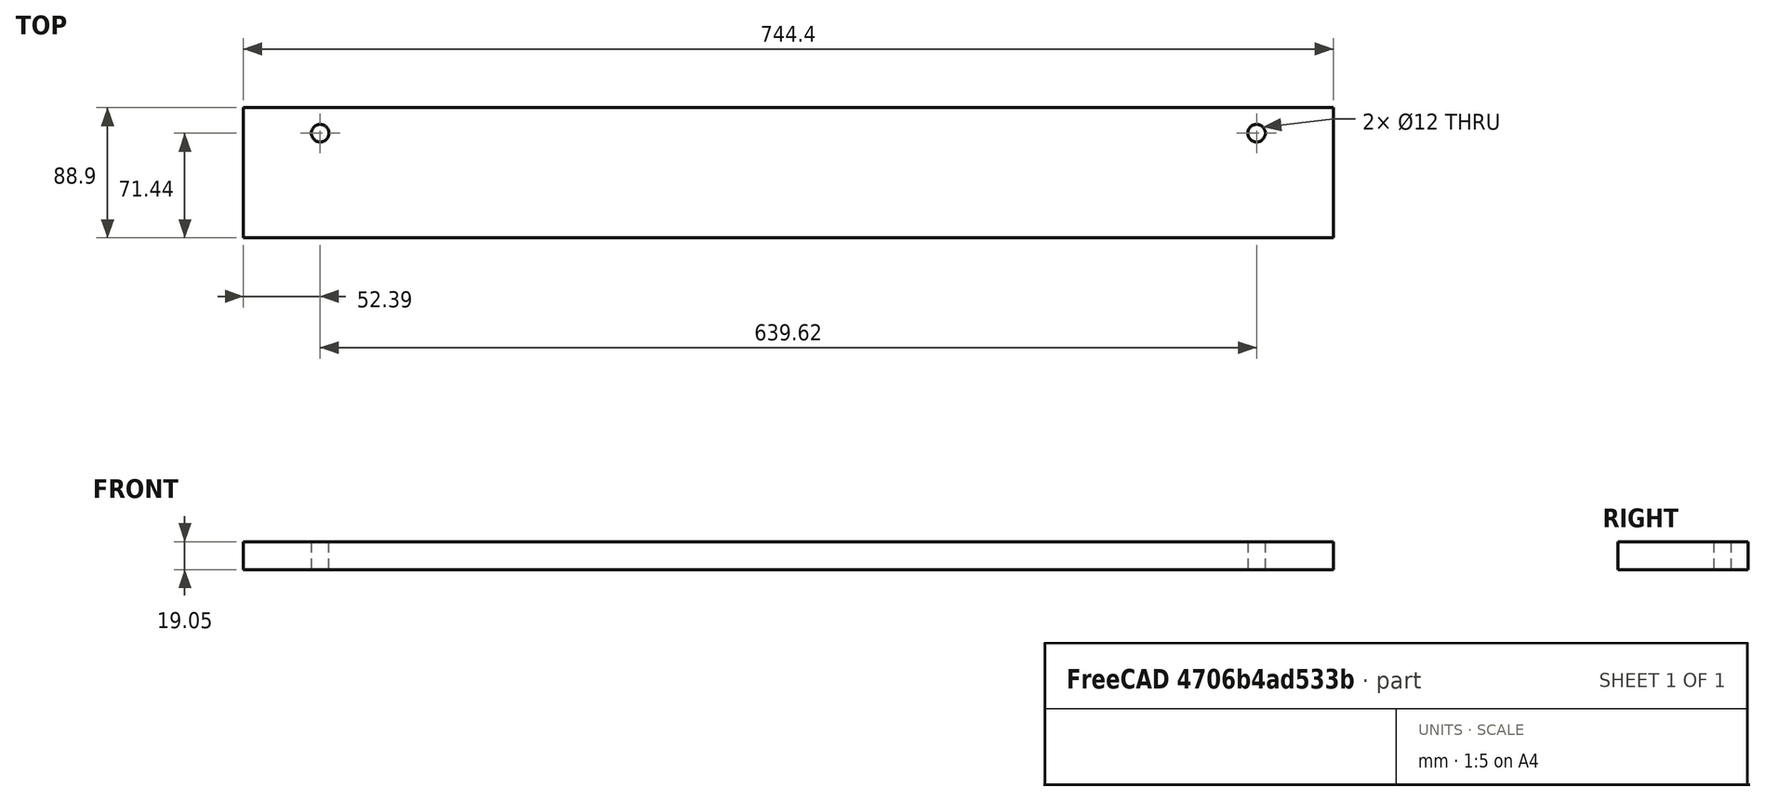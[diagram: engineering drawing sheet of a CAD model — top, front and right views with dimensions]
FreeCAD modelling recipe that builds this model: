
FCSTD DOCUMENT  (FreeCAD 0.19R24291 (Git))
Label: horizontal
License: All rights reserved
LicenseURL: http://en.wikipedia.org/wiki/All_rights_reserved
objects: Sketcher::SketchObject×1, PartDesign::Pad×1, PartDesign::Body×1
note: 4 computed .brp shape members not serialized (recipe doc carries the construction recipe); baked Part::Feature solids carry a one-line shape summary decoded from their .brp

FEATURE [Sketcher::SketchObject] Sketch
  FullyConstrained = true
  MapMode = 5
  Support = -> [XY_Plane]
  expr: Constraints[10] = 3.5 * 25.4
  sketch-geometry (6):
    g0: LineSegment StartX=0 StartY=0 StartZ=0 EndX=744.4 EndY=0 EndZ=0
    g1: LineSegment StartX=744.4 StartY=0 StartZ=0 EndX=744.4 EndY=88.9 EndZ=0
    g2: LineSegment StartX=744.4 StartY=88.9 StartZ=0 EndX=0 EndY=88.9 EndZ=0
    g3: LineSegment StartX=0 StartY=88.9 StartZ=0 EndX=0 EndY=0 EndZ=0
    g4: Circle CenterX=52.39 CenterY=71.44 CenterZ=0 NormalX=0 NormalY=0 NormalZ=1 AngleXU=0 Radius=6
    g5: Circle CenterX=692.01 CenterY=71.44 CenterZ=0 NormalX=0 NormalY=0 NormalZ=1 AngleXU=0 Radius=6
  constraints (17):
    c: Coincident(g0,g1)
    c: Coincident(g1,g2)
    c: Coincident(g2,g3)
    c: Coincident(g3,g0)
    c: Horizontal(g0)
    c: Horizontal(g2)
    c: Vertical(g1)
    c: Vertical(g3)
    c: DistanceX(g0,g0) = 744.4
    c: Coincident(g0,g-1)
    c: DistanceY(g3,g3) = 88.9
    c: DistanceX(g2,g4) = 52.39
    c: DistanceY(g4,g2) = 17.46
    c: Diameter(g4) = 12
    c: Horizontal(g5,g4)
    c: Equal(g5,g4)
    c: DistanceX(g5,g1) = 52.39
FEATURE [PartDesign::Pad] Pad
  Direction = (1,1,1)
  Length = 19.05
  Length2 = 100
  Profile = -> Sketch
  Type = 0
  expr: Length = 3 / 4 * 25.4
FEATURE [PartDesign::Body] Body
  Group = -> [Sketch,Pad]
  Origin = -> Origin
  Tip = -> Pad
